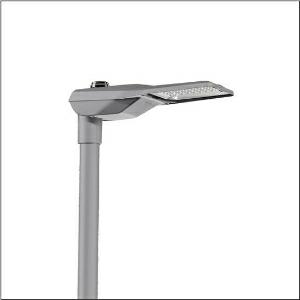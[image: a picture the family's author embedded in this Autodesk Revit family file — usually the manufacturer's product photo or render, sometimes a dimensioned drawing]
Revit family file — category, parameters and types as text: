
# Revit family: streetlight_sl_21_mini___st0_8a_5xe6c47n08jb_51ba
name_source: partatom
category: Lighting Fixtures
units: mm (PartAtom-declared; Revit-internal decimal feet)

## family parameters
Cut with Voids When Loaded = No
Host = Face
Light Source = No
Part Type = Normal
Room Calculation Point = No
Round Connector Dimension = Use Diameter
Shared = No

## types (1)
- --- (1 x LED, 13390 lm, 87.3 W, 4000K)
    Apparent Load = 87 VA
    CIE Flux Codes = 41 75 97 100 100
    Color Rendering = 70
    Color Temperature = 4000K
    Default Elevation = 1800 mm
    Description = Streetlight SL 21 mini, mast luminaire, primary light control with lens, of PMMA, primary optical cover: cover, of toughened safety glass, transparent, light distribution: ST0.8a, light emission: direct distribution, primary light characteristic: asymmetric, installation type: side-entry, LED, 3G 2.5mm², High Power LED, rated luminous flux: 13.390lm, luminous efficacy: 153lm/W, light colour: 740, colour temperature: 4000K, control gear: NEMA (7pin), control: overheat protection, pre-setting: linear dimming characteristic, constant luminous flux control, time-dependent luminous flux control, flexible luminous flux parameterisation, mains connection: 230..240V, AC, 50/60Hz, connection cable pre-assembled, cable length: 10,5m, wiring characteristics: H05VV-F, start of lifetime: 87W, end of service life: 90W, reduction: 40W, luminaire housing, of diecast aluminium (EN AC-44300), powder-coated, SITECO metallic grey (DB 702S), corrosivity category C5 high according to DIN EN ISO 12944, multi-level sealing system, sealing non-destructively replaceable, inclination adjustable: 0°, 5°, 10°, 15°, length: 628mm, width: 235mm, height: 110mm, spigot size: 42mm (side-entry), mounting height: 4..8m, protection rating (complete): IP66, insulation class (complete): insulation class I (protective earthing), certification: CE, ENEC, ENEC+, VDE, impact resistance: IK10, permissible operating ambient temperature for outdoor applications: -40..+50°C, standard-compliant lighting for roads and squares, packaging unit: 1 piece

Light Distribution: ST0.8a
    Height = 110 mm
    Lamp = 1 x LED
    Lamp Light Flux = 13390 lm
    Lamp Power = 87.3 W
    Lamp count = 1
    Length = 625 mm
    Luminous efficacy = 153 lm/W
    Manufacturer = Siteco
    ModVariant = No
    Model = 5XE6C47N08JB
    Number of Poles = 1
    OnlyDefault = Yes
    Power Factor = 1
    Product Name = Streetlight SL 21 mini | ST0.8a
    Product group = mast luminaire | pylon top
    ProductGroupID = 6100
    Protection Class = Protection class I
    Protection Degree = IP 66
    RLX_Detail_Level = 1
    RLX_Emergency_Light_Flux = 0 lm
    RLX_Emergency_Type = 0
    RLX_Emergency_Type_DB = No
    RlxData = <blob elided: 26085 chars, md5=2f373ed2>
    Socket = socket
    Standby Power = 0 W
    System Light Flux = 13390 lm
    System Power = 87 W
    Type Comments = factory setting: luminous flux: 100 % | dim-lin: 254 | 915 mA
    Type Image = l_1294379.jpg
    URL = http://relux.com
    VarID = @adj_133407
    Voltage = 0 V
    Weight = 0.00 kg
    Width = 234 mm

## geometry (parser evidence)
native form markers: Blend x4, Sweep x10
no freeform markers — native parametric forms only
